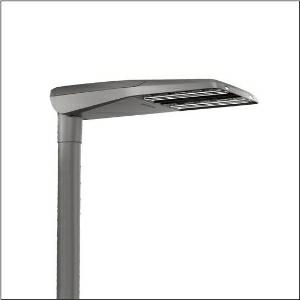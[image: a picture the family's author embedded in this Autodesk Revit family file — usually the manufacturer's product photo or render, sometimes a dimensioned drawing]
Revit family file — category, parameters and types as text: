
# Revit family: streetlight_sl_11_iq_midi___st1_0st0_5_5xc3j51f08me_a600
name_source: partatom
category: Lighting Fixtures
units: mm (PartAtom-declared; Revit-internal decimal feet)

## family parameters
Cut with Voids When Loaded = No
Host = Face
Light Source = No
Part Type = Normal
Room Calculation Point = No
Round Connector Dimension = Use Diameter
Shared = No

## types (1)
- --- (1 x LED, 17650 lm, 124.7 W, 3000K)
    Apparent Load = 125 VA
    CIE Flux Codes = 35 68 96 100 100
    Color Rendering = 70
    Color Temperature = 3000K
    Default Elevation = 1800 mm
    Description = Streetlight SL 11 iQ midi, mast luminaire, primary light control with 3 zone facetted reflector, of plastic, silver coated, highly specular, primary optical cover: cover, of PMMA, transparent, light distribution: ST1.0ST0.5, light emission: direct distribution, primary light characteristic: asymmetric, installation type: post-top, side-entry, lamps: LED, High Power LED, rated values: 17.650lm | 124,7W | 141,5lm/W (begin service life); end service life: 17.650lm | 132,2W; at 50% lumin. flux: 8.825lm | 57,2W | 154,3lm/W, colour temperature: 3000K, colour rendering: CRI > 70, light colour: 730, light setting 1 begin service life: 100% | 17.650lm | 124,7W | 141,5lm/W | 3.000K, light setting 1 end service life: 132,2W, further light settings possible, control: Street-Remote, Auto-Match, Temp-Guard, Lumen-Switch, Night-Set, Smart-Wire, Light-Fading, Desk-Remote (wireless, voltage-free reading and setting of iQ features in the workshop via application-optimized NFC function/RFID function), optimised constant luminous flux control (CLO 2.0), with cable H07RN-F 3x 1.5mm², mains connection: 230..240V, AC, 50/60Hz, connection cable pre-assembled, cable length: 12,5m, luminaire housing, of diecast aluminium, powder-coated, SITECO metallic grey (DB 702S), please order mast flange separately, inclination adjustable without tools: 0°, 5°, 10°, 15° (post-top) | 0°, -5°, -10°, -15° (side-entry), sealing non-destructively replaceable, multi-level sealing system, length: 780mm, width: 376mm, height: 118mm, mast flange for spigot size: 42mm (side-entry): 5XC10008XM4, 60/48mm (side-entry/post-top): 5XC10108XM2, 76/60mm (side-entry/post-top): 5XC10108XM1, equipment: Power, protection rating (complete): IP66, insulation class (complete): insulation class II (safety insulation), certification: CE, ENEC, ENEC+, VDE, impact resistance: IK10, permissible operating ambient temperature for outdoor applications: -25..+50°C, standard-compliant lighting for roads and squares, Environmental Product Declaration (EPD) tested and certified by an independent institute, packaging unit: 1 piece

Light Distribution: ST1.0ST0.5
    Height = 118 mm
    Lamp = 1 x LED
    Lamp Light Flux = 17650 lm
    Lamp Power = 124.7 W
    Lamp count = 1
    Length = 780 mm
    Luminous efficacy = 142 lm/W
    Manufacturer = Siteco
    ModVariant = No
    Model = 5XC3J51F08ME
    Number of Poles = 1
    OnlyDefault = Yes
    Power Factor = 1
    Product Name = Streetlight SL 11 iQ midi | ST1.0ST0.5
    Product group = mast luminaire | pylon top
    ProductGroupID = 6100
    Protection Class = Protection class II
    Protection Degree = IP 66
    RLX_Detail_Level = 1
    RLX_Emergency_Light_Flux = 0 lm
    RLX_Emergency_Type = 0
    RLX_Emergency_Type_DB = No
    RlxData = <blob elided: 70761 chars, md5=190960d4>
    Socket = socket
    Standby Power = 0 W
    System Light Flux = 17650 lm
    System Power = 125 W
    Type Comments = factory setting: luminous flux: 100 % | dim-lin: 254 | 557 mA
    Type Image = l_1005960.jpg
    URL = http://relux.com
    VarID = @adj_047777
    Voltage = 0 V
    Weight = 0.00 kg
    Width = 376 mm

## geometry (parser evidence)
native form markers: Blend x4, Sweep x9
no freeform markers — native parametric forms only
